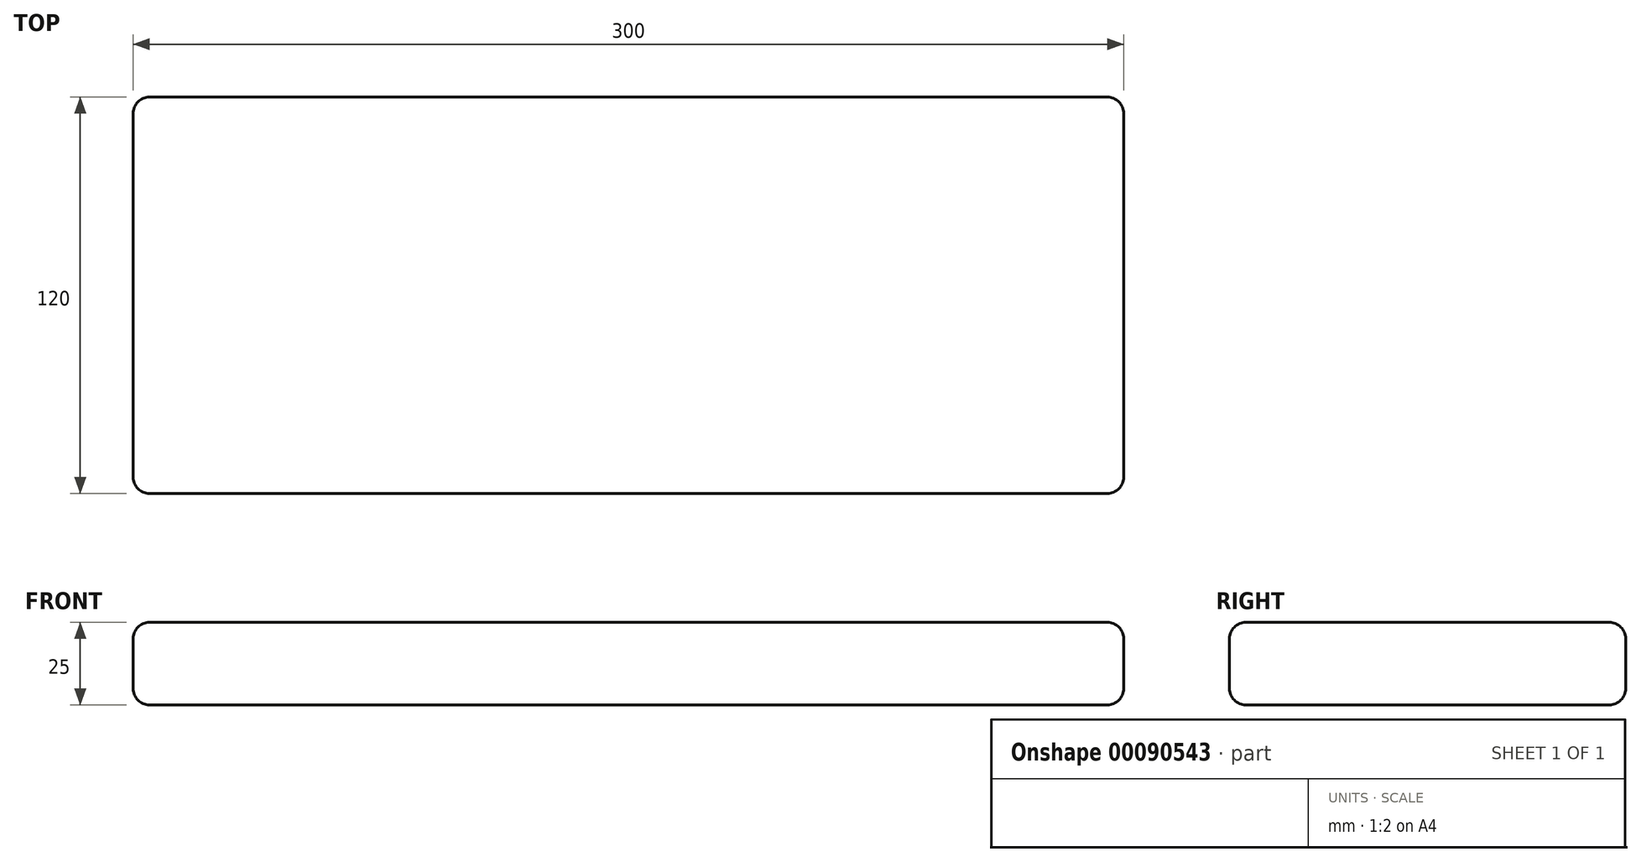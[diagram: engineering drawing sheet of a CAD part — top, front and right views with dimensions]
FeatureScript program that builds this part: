
annotation { "Feature Type Name" : "Feature", "Feature Type Description" : "" }
export const myFeature = defineFeature(function(context is Context, id is Id, definition is map)
    precondition{}
    {
        {
            var Q0;
            Q0=qCreatedBy(makeId("Top.planeOp"),FACE);
            var sketch = newSketch(context, id + "F0", { "sketchPlane" : qUnion([Q0])});
            skLineSegment(sketch, "E0.bottom", {"start": v(150, -60) * mm, "end": v(-150, -60) * mm});
            skLineSegment(sketch, "E0.top", {"start": v(150, 60) * mm, "end": v(-150, 60) * mm});
            skLineSegment(sketch, "E0.left", {"start": v(150, -60) * mm, "end": v(150, 60) * mm});
            skLineSegment(sketch, "E0.right", {"start": v(-150, -60) * mm, "end": v(-150, 60) * mm});
            skPoint(sketch, "E0.middle", {"position": v(0, 0) * mm});
            skSolve(sketch);
        }
        {
            var Q0;
            Q0=makeQuery(id+"F0.imprint","IMPRINT",FACE,{"disambiguationData":[TD([[makeQuery(id+"F0.imprint","IMPRINT",EDGE,{"derivedFrom":sQuery(id+"F0.wireOp",EDGE,"E0.bottom")}),-1.0]])]});
            extrude(context, id + "F1", {"entities" : qUnion([Q0]), "depth" : 25 * mm});
        }
        {
            var Q0;
            Q0=makeQuery(id+"F1.opExtrude","SWEPT_EDGE",EDGE,{"disambiguationData":[OSD([sQuery(id+"F0.wireOp",EDGE,"E0.bottom"),sQuery(id+"F0.wireOp",EDGE,"E0.left")])]});
            var Q1;
            Q1=makeQuery(id+"F1.opExtrude","SWEPT_EDGE",EDGE,{"disambiguationData":[OSD([sQuery(id+"F0.wireOp",EDGE,"E0.top"),sQuery(id+"F0.wireOp",EDGE,"E0.left")])]});
            var Q2;
            Q2=makeQuery(id+"F1.opExtrude","SWEPT_EDGE",EDGE,{"disambiguationData":[OSD([sQuery(id+"F0.wireOp",EDGE,"E0.bottom"),sQuery(id+"F0.wireOp",EDGE,"E0.right")])]});
            var Q3;
            Q3=makeQuery(id+"F1.opExtrude","SWEPT_EDGE",EDGE,{"disambiguationData":[OSD([sQuery(id+"F0.wireOp",EDGE,"E0.top"),sQuery(id+"F0.wireOp",EDGE,"E0.right")])]});
            fillet(context, id + "F2", {"entities" : qUnion([Q0, Q1, Q2, Q3]), "radius" : 5 * mm, "tangentPropagation" : true, "allowEdgeOverflow" : false});
        }
        {
            var Q0;
            Q0=makeQuery(id+"F1.opExtrude","CAP_EDGE",EDGE,{"disambiguationData":[OSD([sQuery(id+"F0.wireOp",EDGE,"E0.bottom")])],"isStart":true});
            var Q1;
            Q1=makeQuery(id+"F1.opExtrude","CAP_EDGE",EDGE,{"disambiguationData":[OSD([sQuery(id+"F0.wireOp",EDGE,"E0.bottom")])],"isStart":false});
            fillet(context, id + "F3", {"entities" : qUnion([Q0, Q1]), "radius" : 5 * mm, "tangentPropagation" : true, "allowEdgeOverflow" : false});
        }
    });
